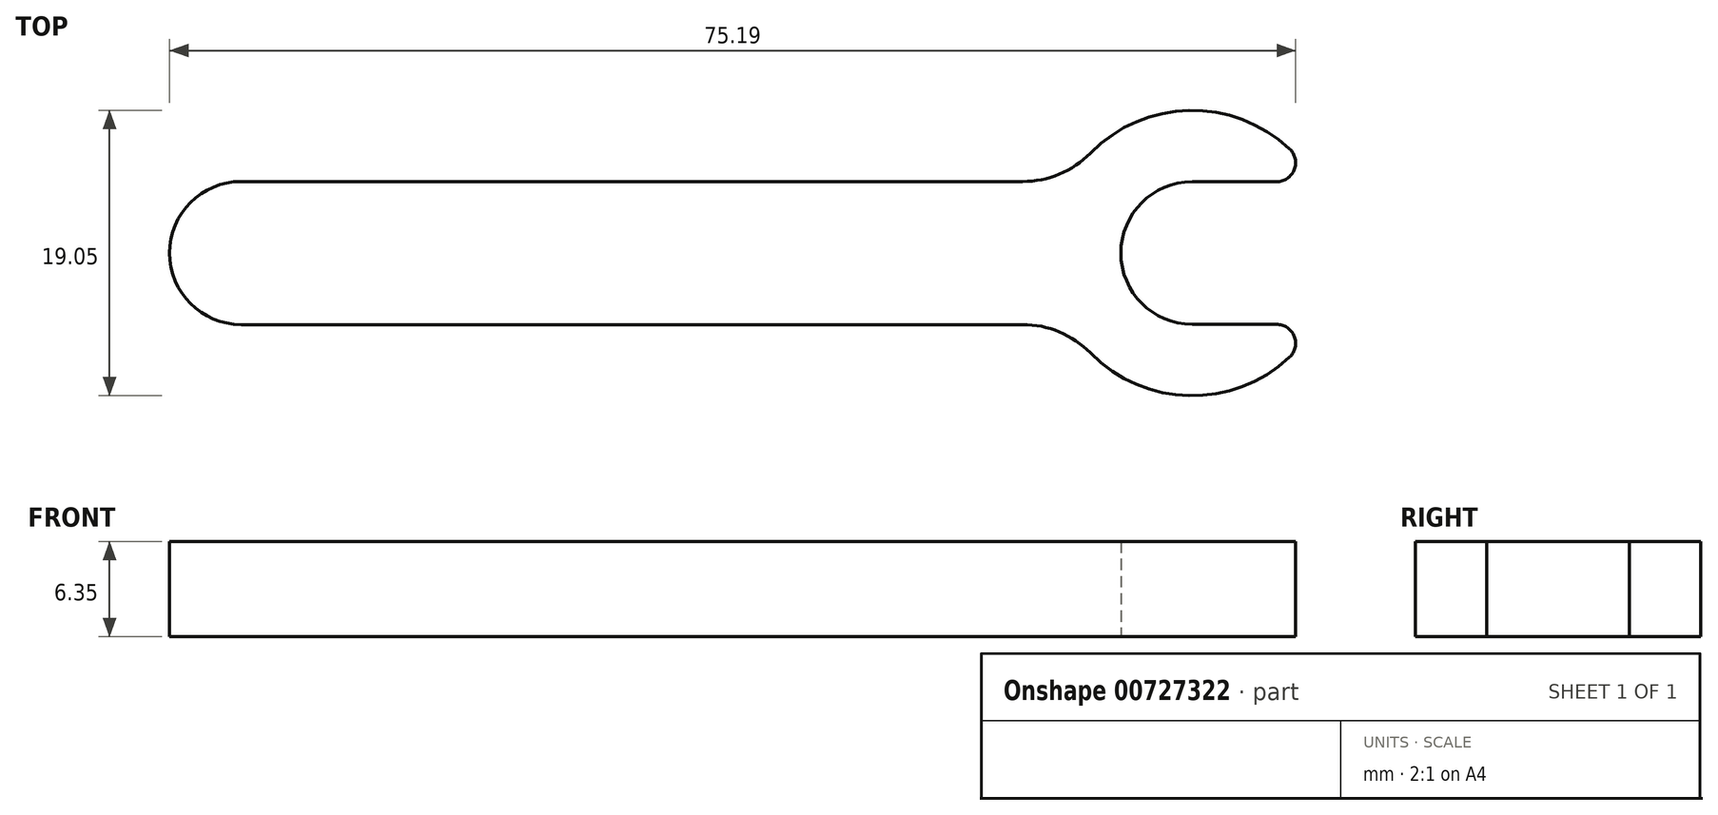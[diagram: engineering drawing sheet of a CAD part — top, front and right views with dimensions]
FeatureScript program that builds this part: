
annotation { "Feature Type Name" : "Feature", "Feature Type Description" : "" }
export const myFeature = defineFeature(function(context is Context, id is Id, definition is map)
    precondition{}
    {
        {
            var Q0;
            Q0=qCreatedBy(makeId("Top.planeOp"),FACE);
            var sketch = newSketch(context, id + "F0", { "sketchPlane" : qUnion([Q0])});
            skLineSegment(sketch, "E0", {"start": v(0, 0) * mm, "end": v(63.5, 0) * mm, "construction": true});
            skArc(sketch, "E1", {"start": v(0, 4.78) * mm, "mid": v(-4.78, 0) * mm, "end": v(0, -4.78) * mm});
            skLineSegment(sketch, "E2", {"start": v(0, 4.78) * mm, "end": v(52.18, 4.78) * mm});
            skLineSegment(sketch, "E3", {"start": v(0, -4.78) * mm, "end": v(52.18, -4.78) * mm});
            skArc(sketch, "E4", {"start": v(70, 6.96) * mm, "mid": v(63.3, 9.52) * mm, "end": v(56.7, 6.68) * mm});
            skArc(sketch, "E5", {"start": v(63.5, 4.76) * mm, "mid": v(58.74, 0) * mm, "end": v(63.5, -4.76) * mm});
            skLineSegment(sketch, "E6", {"start": v(63.5, 4.76) * mm, "end": v(69.14, 4.76) * mm});
            skLineSegment(sketch, "E7", {"start": v(63.5, -4.76) * mm, "end": v(69.14, -4.76) * mm});
            skArc(sketch, "E8", {"start": v(69.14, 4.76) * mm, "mid": v(70.32, 5.57) * mm, "end": v(70, 6.96) * mm});
            skArc(sketch, "E9", {"start": v(70, -6.96) * mm, "mid": v(70.32, -5.57) * mm, "end": v(69.14, -4.76) * mm});
            skArc(sketch, "E10", {"start": v(56.7, -6.68) * mm, "mid": v(63.3, -9.52) * mm, "end": v(70, -6.96) * mm});
            skPoint(sketch, "E11.visualSharp", {"position": v(55.26, 4.78) * mm});
            skArc(sketch, "E11.filletArc", {"start": v(52.18, 4.78) * mm, "mid": v(54.63, 5.27) * mm, "end": v(56.7, 6.68) * mm});
            skPoint(sketch, "E12.visualSharp", {"position": v(55.26, -4.78) * mm});
            skArc(sketch, "E12.filletArc", {"start": v(56.7, -6.68) * mm, "mid": v(54.63, -5.27) * mm, "end": v(52.18, -4.78) * mm});
            skSolve(sketch);
        }
        {
            var Q0;
            Q0=makeQuery(id+"F0.imprint","IMPRINT",FACE,{"disambiguationData":[TD([[makeQuery(id+"F0.imprint","IMPRINT",EDGE,{"derivedFrom":sQuery(id+"F0.wireOp",EDGE,"E1")}),1.0]])]});
            extrude(context, id + "F1", {"entities" : qUnion([Q0]), "depth" : 6.35 * mm, "offsetDistance" : 25.4 * mm});
        }
    });
